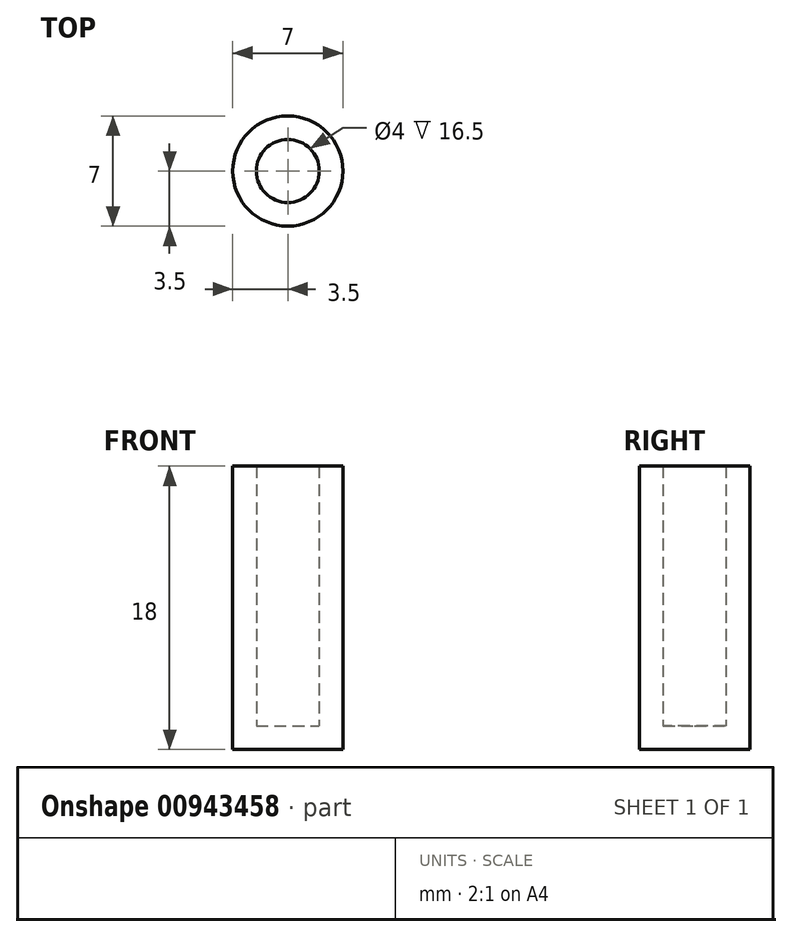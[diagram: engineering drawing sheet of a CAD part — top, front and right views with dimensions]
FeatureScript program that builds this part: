
annotation { "Feature Type Name" : "Feature", "Feature Type Description" : "" }
export const myFeature = defineFeature(function(context is Context, id is Id, definition is map)
    precondition{}
    {
        {
            var Q0;
            Q0=qCreatedBy(makeId("Front.planeOp"),FACE);
            var sketch = newSketch(context, id + "F0", { "sketchPlane" : qUnion([Q0])});
            skLineSegment(sketch, "E0.bottom", {"start": v(0, 0) * mm, "end": v(2, 0) * mm});
            skLineSegment(sketch, "E0.top", {"start": v(0, 1.5) * mm, "end": v(2, 1.5) * mm});
            skLineSegment(sketch, "E0.left", {"start": v(0, 0) * mm, "end": v(0, 1.5) * mm});
            skLineSegment(sketch, "E1.bottom", {"start": v(2, 0) * mm, "end": v(3.5, 0) * mm});
            skLineSegment(sketch, "E1.top", {"start": v(2, 18) * mm, "end": v(3.5, 18) * mm});
            skLineSegment(sketch, "E1.left", {"start": v(2, 1.5) * mm, "end": v(2, 18) * mm});
            skLineSegment(sketch, "E1.right", {"start": v(3.5, 0) * mm, "end": v(3.5, 18) * mm});
            skSolve(sketch);
        }
        {
            var Q0;
            Q0=makeQuery(id+"F0.imprint","IMPRINT",FACE,{"disambiguationData":[TD([[makeQuery(id+"F0.imprint","IMPRINT",EDGE,{"derivedFrom":sQuery(id+"F0.wireOp",EDGE,"E0.bottom")}),1.0]])]});
            var Q1;
            Q1=sQuery(id+"F0.wireOp",EDGE,"E0.left");
            revolve(context, id + "F1", {"surfaceOperationType" : NewSurfaceOperationType.NEW, "entities" : qUnion([Q0]), "axis" : qUnion([Q1]), "revolveType" : RevolveType.FULL});
        }
    });
